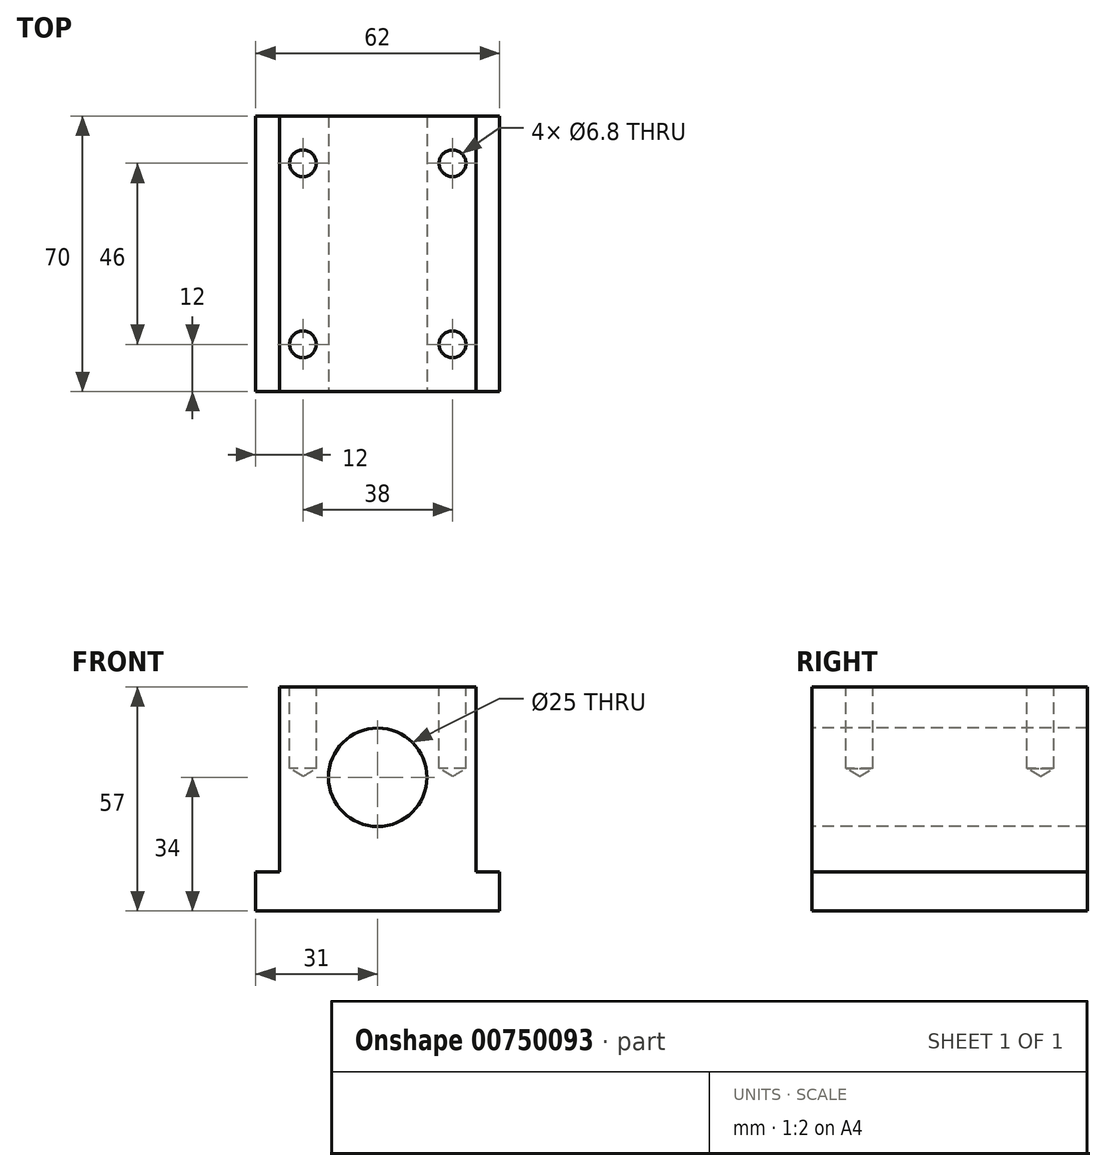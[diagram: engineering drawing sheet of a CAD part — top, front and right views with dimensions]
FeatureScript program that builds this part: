
annotation { "Feature Type Name" : "Feature", "Feature Type Description" : "" }
export const myFeature = defineFeature(function(context is Context, id is Id, definition is map)
    precondition{}
    {
        {
            var Q0;
            Q0=qCreatedBy(makeId("Front.planeOp"),FACE);
            var sketch = newSketch(context, id + "F0", { "sketchPlane" : qUnion([Q0])});
            skLineSegment(sketch, "E0", {"start": v(0, 23) * mm, "end": v(25, 23) * mm});
            skLineSegment(sketch, "E1", {"start": v(25, 23) * mm, "end": v(25, -24) * mm});
            skLineSegment(sketch, "E2", {"start": v(25, -24) * mm, "end": v(31, -24) * mm});
            skLineSegment(sketch, "E3", {"start": v(31, -24) * mm, "end": v(31, -34) * mm});
            skLineSegment(sketch, "E4", {"start": v(31, -34) * mm, "end": v(0, -34) * mm});
            skLineSegment(sketch, "E5", {"start": v(0, -34) * mm, "end": v(0, 23) * mm, "construction": true});
            skLineSegment(sketch, "E6.MirrorCS", {"start": v(-25, -24) * mm, "end": v(-31, -24) * mm});
            skLineSegment(sketch, "E7.MirrorCS", {"start": v(-31, -34) * mm, "end": v(0, -34) * mm});
            skLineSegment(sketch, "E8.MirrorCS", {"start": v(-31, -24) * mm, "end": v(-31, -34) * mm});
            skLineSegment(sketch, "E9.MirrorCS", {"start": v(0, 23) * mm, "end": v(-25, 23) * mm});
            skLineSegment(sketch, "E10.MirrorCS", {"start": v(-25, 23) * mm, "end": v(-25, -24) * mm});
            skCircle(sketch, "E11", {"center": v(0, 0) * mm, "radius": 12.5 * mm});
            skSolve(sketch);
        }
        {
            var Q0;
            Q0=makeQuery(id+"F0.imprint","IMPRINT",FACE,{"disambiguationData":[TD([[makeQuery(id+"F0.imprint","IMPRINT",EDGE,{"derivedFrom":sQuery(id+"F0.wireOp",EDGE,"E0")}),-1.0]])]});
            extrude(context, id + "F1", {"entities" : qUnion([Q0]), "oppositeDirection" : true, "depth" : 70 * mm, "offsetDistance" : 25 * mm});
        }
        {
            var Q0;
            Q0=makeQuery(id+"F1.opExtrude","SWEPT_FACE",FACE,{"disambiguationData":[OSD([sQuery(id+"F0.wireOp",EDGE,"E0"),sQuery(id+"F0.wireOp",EDGE,"E9.MirrorCS")])]});
            var sketch = newSketch(context, id + "F2", { "sketchPlane" : qUnion([Q0])});
            skPoint(sketch, "E12", {"position": v(-19, 58) * mm});
            skPoint(sketch, "E13", {"position": v(19, 58) * mm});
            skPoint(sketch, "E14", {"position": v(-19, 12) * mm});
            skPoint(sketch, "E15", {"position": v(19, 12) * mm});
            skSolve(sketch);
        }
        {
            var Q0;
            Q0=sQuery(id+"F2.wireOp",VERTEX,"E12");
            var Q1;
            Q1=sQuery(id+"F2.wireOp",VERTEX,"E14");
            var Q2;
            Q2=sQuery(id+"F2.wireOp",VERTEX,"E15");
            var Q3;
            Q3=sQuery(id+"F2.wireOp",VERTEX,"E13");
            var Q4;
            Q4=makeQuery(id+"F1.opExtrude","SWEPT_BODY",BODY,{"disambiguationData":[OSD([sQuery(id+"F0.wireOp",EDGE,"E0"),sQuery(id+"F0.wireOp",EDGE,"E1"),sQuery(id+"F0.wireOp",EDGE,"E2"),sQuery(id+"F0.wireOp",EDGE,"E3"),sQuery(id+"F0.wireOp",EDGE,"E4"),sQuery(id+"F0.wireOp",EDGE,"E6.MirrorCS"),sQuery(id+"F0.wireOp",EDGE,"E7.MirrorCS"),sQuery(id+"F0.wireOp",EDGE,"E8.MirrorCS"),sQuery(id+"F0.wireOp",EDGE,"E9.MirrorCS"),sQuery(id+"F0.wireOp",EDGE,"E10.MirrorCS"),sQuery(id+"F0.wireOp",EDGE,"E11")])]});
            hole(context, id + "F3", {"style" : HoleStyle.SIMPLE, "endStyle" : HoleEndStyle.BLIND, "standardTappedOrClearance" : lookupTablePath({ "standard" : "ISO", "engagement" : "75%", "pitch" : "1.25 mm", "size" : "M8", "type" : "Tapped" }), "standardBlindInLast" : lookupTablePath({ "standard" : "ISO", "engagement" : "75%", "pitch" : "1.25 mm", "size" : "M8", "type" : "Tapped" }), "holeDiameter" : 6.8 * mm, "majorDiameter" : 8 * mm, "showTappedDepth" : true, "holeDepth" : 20.75 * mm, "isTappedThrough" : true, "tappedDepth" : 12 * mm, "tapClearance" : 7, "locations" : qUnion([Q0, Q1, Q2, Q3]), "scope" : qUnion([Q4])});
        }
    });
